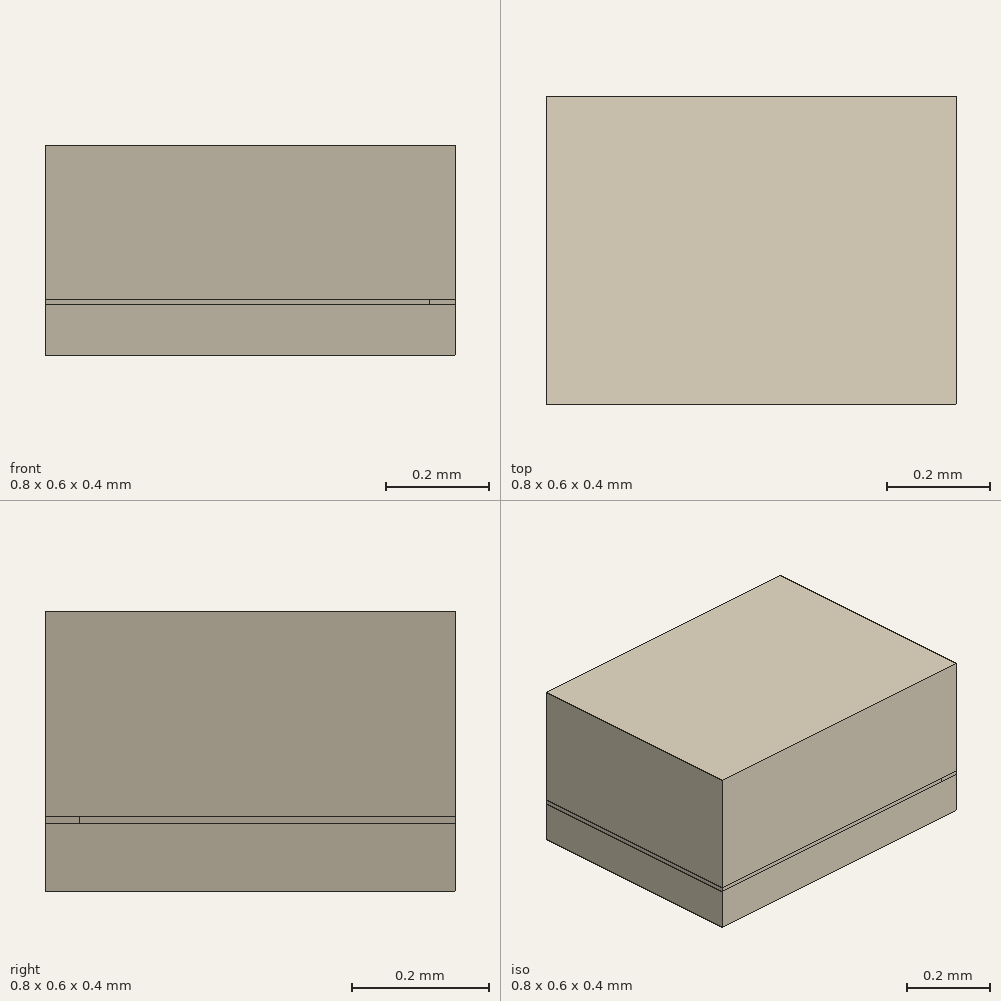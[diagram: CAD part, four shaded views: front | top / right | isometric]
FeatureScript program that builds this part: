
annotation { "Feature Type Name" : "Feature", "Feature Type Description" : "" }
export const myFeature = defineFeature(function(context is Context, id is Id, definition is map)
    precondition{}
    {
        {
            var Q0;
            Q0=qCreatedBy(makeId("Top.planeOp"),FACE);
            var sketch = newSketch(context, id + "F0", { "sketchPlane" : qUnion([Q0])});
            skLineSegment(sketch, "E0.bottom", {"start": v(0, 0) * mm, "end": v(-0.8, 0) * mm});
            skLineSegment(sketch, "E0.top", {"start": v(0, 0.6) * mm, "end": v(-0.8, 0.6) * mm});
            skLineSegment(sketch, "E0.left", {"start": v(0, 0) * mm, "end": v(0, 0.6) * mm});
            skLineSegment(sketch, "E0.right", {"start": v(-0.8, 0) * mm, "end": v(-0.8, 0.6) * mm});
            skSolve(sketch);
        }
        {
            var Q0;
            Q0 = qSketchRegion(id + "F0", true);
            extrude(context, id + "F1", {"entities" : qUnion([Q0]), "depth" : 0.1 * mm, "offsetDistance" : 25.4 * mm});
        }
        {
            var Q0;
            Q0=makeQuery(id+"F1.opExtrude","CAP_FACE",FACE,{"disambiguationData":[OSD([sQuery(id+"F0.wireOp",EDGE,"E0.bottom"),sQuery(id+"F0.wireOp",EDGE,"E0.top"),sQuery(id+"F0.wireOp",EDGE,"E0.left"),sQuery(id+"F0.wireOp",EDGE,"E0.right")])],"isStart":false});
            var sketch = newSketch(context, id + "F2", { "sketchPlane" : qUnion([Q0])});
            skLineSegment(sketch, "E1.bottom", {"start": v(0, 0) * mm, "end": v(-0.05, 0) * mm});
            skLineSegment(sketch, "E1.top", {"start": v(0, 0.05) * mm, "end": v(-0.05, 0.05) * mm});
            skLineSegment(sketch, "E1.left", {"start": v(0, 0) * mm, "end": v(0, 0.05) * mm});
            skLineSegment(sketch, "E1.right", {"start": v(-0.05, 0) * mm, "end": v(-0.05, 0.05) * mm});
            skSolve(sketch);
        }
        {
            var Q0;
            Q0 = qSketchRegion(id + "F2", true);
            extrude(context, id + "F3", {"entities" : qUnion([Q0]), "depth" : 0.01 * mm, "offsetDistance" : 25.4 * mm});
        }
        {
            var Q0;
            Q0=makeQuery(id+"F1.opExtrude","CAP_FACE",FACE,{"disambiguationData":[OSD([sQuery(id+"F0.wireOp",EDGE,"E0.bottom"),sQuery(id+"F0.wireOp",EDGE,"E0.top"),sQuery(id+"F0.wireOp",EDGE,"E0.left"),sQuery(id+"F0.wireOp",EDGE,"E0.right")])],"isStart":false});
            var sketch = newSketch(context, id + "F4", { "sketchPlane" : qUnion([Q0])});
            skLineSegment(sketch, "E2", {"start": v(-0.8, 0.6) * mm, "end": v(-0.8, 0) * mm});
            skLineSegment(sketch, "E3", {"start": v(-0.8, 0) * mm, "end": v(-0.05, 0) * mm});
            skLineSegment(sketch, "E4", {"start": v(-0.05, 0) * mm, "end": v(-0.05, 0.05) * mm});
            skLineSegment(sketch, "E5", {"start": v(-0.05, 0.05) * mm, "end": v(0, 0.05) * mm});
            skLineSegment(sketch, "E6", {"start": v(0, 0.05) * mm, "end": v(0, 0.6) * mm});
            skLineSegment(sketch, "E7", {"start": v(0, 0.6) * mm, "end": v(-0.8, 0.6) * mm});
            skSolve(sketch);
        }
        {
            var Q0;
            Q0 = qSketchRegion(id + "F4", true);
            extrude(context, id + "F5", {"entities" : qUnion([Q0]), "depth" : 0.01 * mm, "offsetDistance" : 25.4 * mm});
        }
        {
            var Q0;
            Q0=makeQuery(id+"F5.opExtrude","CAP_FACE",FACE,{"disambiguationData":[OSD([sQuery(id+"F4.wireOp",EDGE,"E2"),sQuery(id+"F4.wireOp",EDGE,"E3"),sQuery(id+"F4.wireOp",EDGE,"E4"),sQuery(id+"F4.wireOp",EDGE,"E5"),sQuery(id+"F4.wireOp",EDGE,"E6"),sQuery(id+"F4.wireOp",EDGE,"E7")])],"isStart":false});
            var sketch = newSketch(context, id + "F6", { "sketchPlane" : qUnion([Q0])});
            skLineSegment(sketch, "E8.bottom", {"start": v(0, 0) * mm, "end": v(-0.8, 0) * mm});
            skLineSegment(sketch, "E8.top", {"start": v(0, 0.6) * mm, "end": v(-0.8, 0.6) * mm});
            skLineSegment(sketch, "E8.left", {"start": v(0, 0) * mm, "end": v(0, 0.6) * mm});
            skLineSegment(sketch, "E8.right", {"start": v(-0.8, 0) * mm, "end": v(-0.8, 0.6) * mm});
            skSolve(sketch);
        }
        {
            var Q0;
            Q0 = qSketchRegion(id + "F6", true);
            extrude(context, id + "F7", {"entities" : qUnion([Q0]), "depth" : 0.3 * mm, "offsetDistance" : 25.4 * mm});
        }
    });
